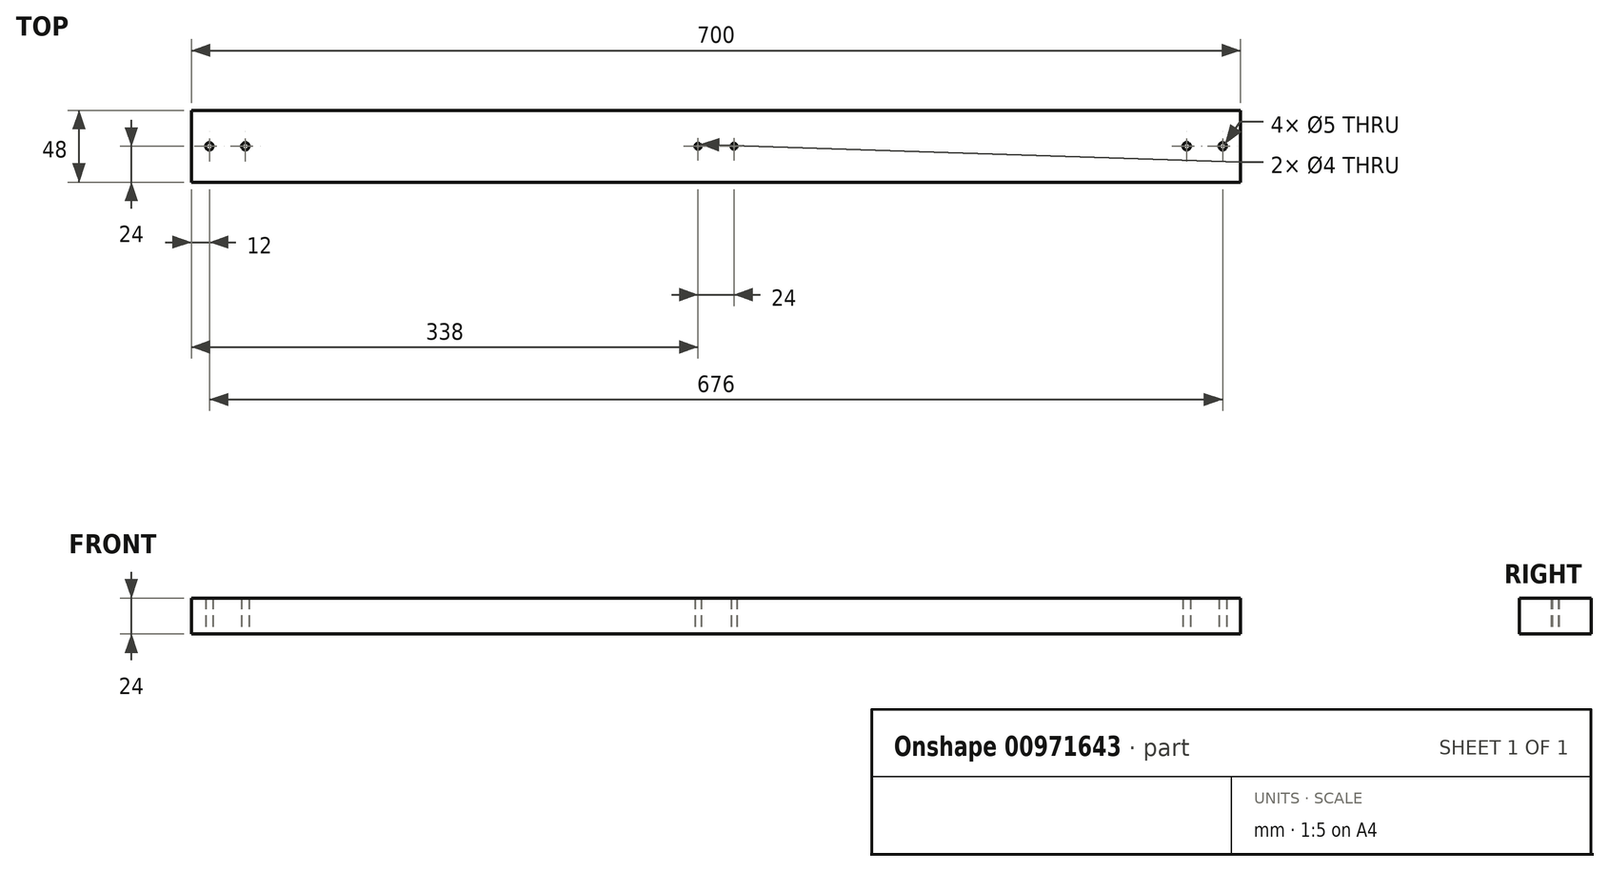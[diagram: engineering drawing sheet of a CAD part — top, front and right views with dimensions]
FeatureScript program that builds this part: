
annotation { "Feature Type Name" : "Feature", "Feature Type Description" : "" }
export const myFeature = defineFeature(function(context is Context, id is Id, definition is map)
    precondition{}
    {
        {
            assignVariable(context, id + "F0", {"name" : "a", "anyValue" : 24});
        }
        {
            var Q0;
            Q0=qCreatedBy(makeId("Top.planeOp"),FACE);
            var sketch = newSketch(context, id + "F1", { "sketchPlane" : qUnion([Q0])});
            skLineSegment(sketch, "E0.bottom", {"start": v(350, -24) * mm, "end": v(-350, -24) * mm});
            skLineSegment(sketch, "E0.top", {"start": v(350, 24) * mm, "end": v(-350, 24) * mm});
            skLineSegment(sketch, "E0.left", {"start": v(350, -24) * mm, "end": v(350, 24) * mm});
            skLineSegment(sketch, "E0.right", {"start": v(-350, -24) * mm, "end": v(-350, 24) * mm});
            skPoint(sketch, "E0.middle", {"position": v(0, 0) * mm});
            skLineSegment(sketch, "E1", {"start": v(350, 0) * mm, "end": v(338, 0) * mm});
            skLineSegment(sketch, "E2", {"start": v(338, 0) * mm, "end": v(314, 0) * mm});
            skCircle(sketch, "E3", {"center": v(338, 0) * mm, "radius": 2.5 * mm});
            skCircle(sketch, "E4", {"center": v(314, 0) * mm, "radius": 2.5 * mm});
            skCircle(sketch, "E5.MirrorC", {"center": v(-314, 0) * mm, "radius": 2.5 * mm});
            skCircle(sketch, "E6.MirrorC", {"center": v(-338, 0) * mm, "radius": 2.5 * mm});
            skLineSegment(sketch, "E7", {"start": v(0, 0) * mm, "end": v(12, 0) * mm});
            skLineSegment(sketch, "E8", {"start": v(0, 0) * mm, "end": v(-12, 0) * mm});
            skCircle(sketch, "E9", {"center": v(12, 0) * mm, "radius": 2 * mm});
            skCircle(sketch, "E10", {"center": v(-12, 0) * mm, "radius": 2 * mm});
            skSolve(sketch);
        }
        {
            var Q0;
            {var subQ3=sQuery(id+"F1.wireOp",EDGE,"E0.bottom");Q0=makeQuery(id+"F1.imprint","IMPRINT",FACE,{"disambiguationData":[TD([[makeQuery(id+"F1.imprint","IMPRINT",EDGE,{"derivedFrom":subQ3}),-1.0]])]});}
            extrude(context, id + "F2", {"entities" : qUnion([Q0]), "depth" : (getVariable(context, 'a')) * mm, "offsetDistance" : 25 * mm});
        }
    });
